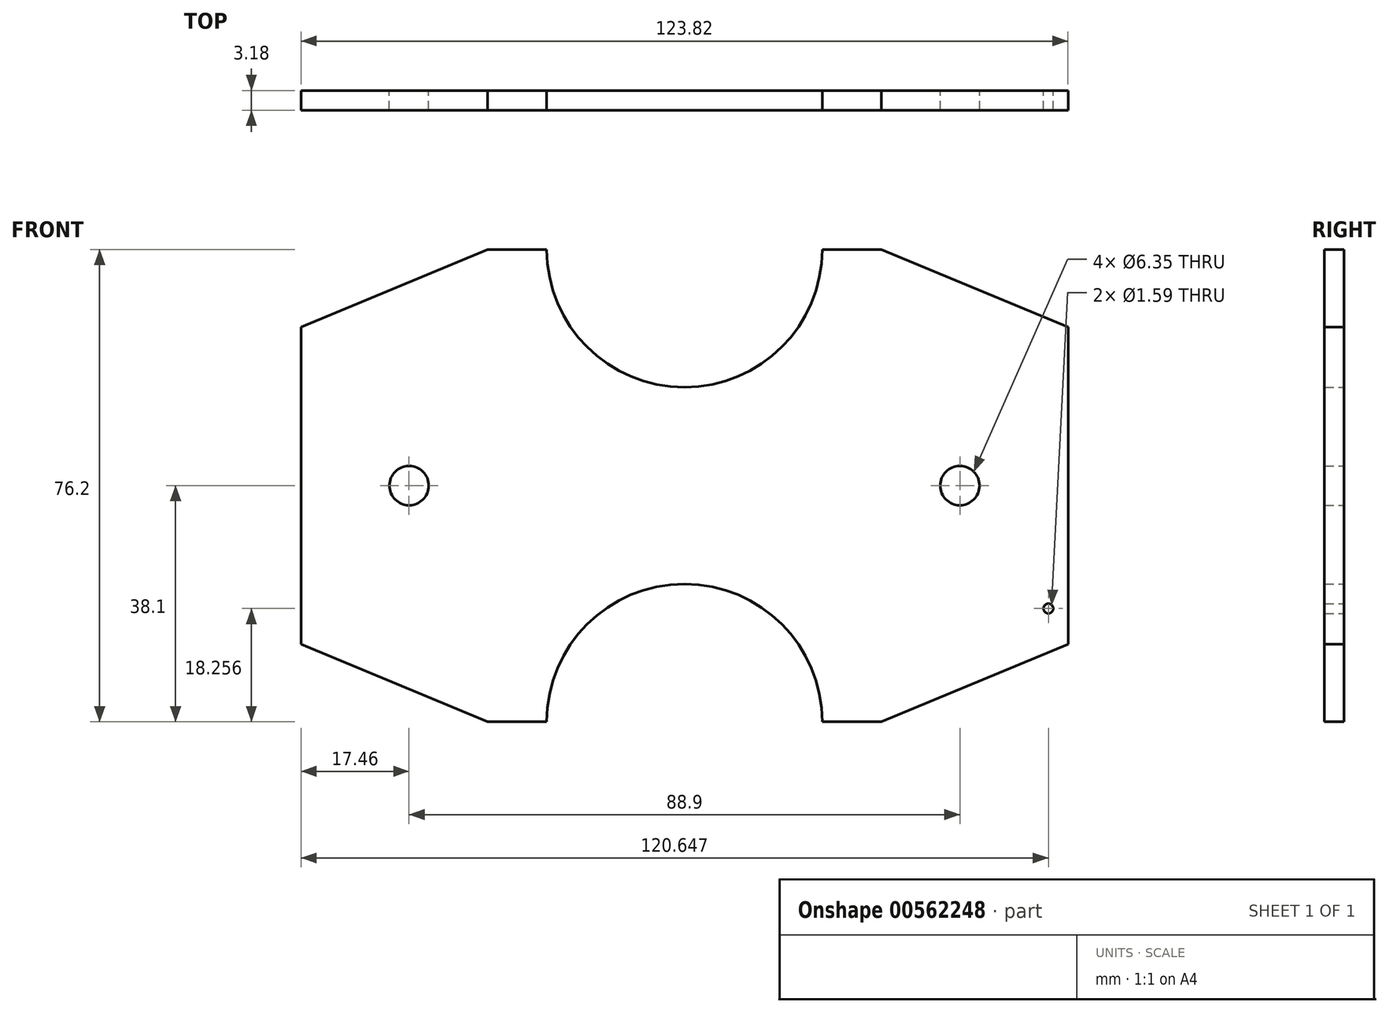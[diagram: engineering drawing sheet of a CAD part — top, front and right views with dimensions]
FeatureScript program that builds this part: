
annotation { "Feature Type Name" : "Feature", "Feature Type Description" : "" }
export const myFeature = defineFeature(function(context is Context, id is Id, definition is map)
    precondition{}
    {
        {
            var Q0;
            Q0=qCreatedBy(makeId("Front.planeOp"),FACE);
            var sketch = newSketch(context, id + "F0", { "sketchPlane" : qUnion([Q0])});
            skLineSegment(sketch, "E0.bottom", {"start": v(-31.75, 38.1) * mm, "end": v(-22.23, 38.1) * mm});
            skLineSegment(sketch, "E0.top", {"start": v(-31.75, -38.1) * mm, "end": v(-22.23, -38.1) * mm});
            skLineSegment(sketch, "E0.left", {"start": v(-61.91, 25.6) * mm, "end": v(-61.91, -25.6) * mm});
            skLineSegment(sketch, "E0.right", {"start": v(0, 38.1) * mm, "end": v(0, -38.1) * mm, "construction": true});
            skLineSegment(sketch, "E1", {"start": v(-61.91, -25.6) * mm, "end": v(-31.75, -38.1) * mm});
            skArc(sketch, "E2", {"start": v(-22.23, 38.1) * mm, "mid": v(-15.72, 22.38) * mm, "end": v(0, 15.88) * mm});
            skLineSegment(sketch, "E3", {"start": v(-31.75, 38.1) * mm, "end": v(-61.91, 25.6) * mm});
            skArc(sketch, "E4.MirrorCS", {"start": v(-22.23, -38.1) * mm, "mid": v(-15.72, -22.38) * mm, "end": v(0, -15.88) * mm});
            skArc(sketch, "E5.MirrorCS", {"start": v(22.23, -38.1) * mm, "mid": v(15.72, -22.38) * mm, "end": v(0, -15.88) * mm});
            skLineSegment(sketch, "E6.MirrorCS", {"start": v(31.75, -38.1) * mm, "end": v(22.23, -38.1) * mm});
            skLineSegment(sketch, "E7.MirrorCS", {"start": v(61.91, -25.6) * mm, "end": v(31.75, -38.1) * mm});
            skLineSegment(sketch, "E8.MirrorCS", {"start": v(61.91, 25.6) * mm, "end": v(61.91, -25.6) * mm});
            skLineSegment(sketch, "E9.MirrorCS", {"start": v(31.75, 38.1) * mm, "end": v(61.91, 25.6) * mm});
            skLineSegment(sketch, "E10.MirrorCS", {"start": v(31.75, 38.1) * mm, "end": v(22.23, 38.1) * mm});
            skArc(sketch, "E11.MirrorCS", {"start": v(22.23, 38.1) * mm, "mid": v(15.72, 22.38) * mm, "end": v(0, 15.88) * mm});
            skCircle(sketch, "E12", {"center": v(44.45, 0) * mm, "radius": 3.18 * mm});
            skCircle(sketch, "E13", {"center": v(58.74, -19.84) * mm, "radius": 0.8 * mm});
            skCircle(sketch, "E14.MirrorC", {"center": v(-44.45, 0) * mm, "radius": 3.18 * mm});
            skSolve(sketch);
        }
        {
            var Q0;
            Q0 = qSketchRegion(id + "F0", true);
            extrude(context, id + "F1", {"entities" : qUnion([Q0]), "depth" : 3.17 * mm, "offsetDistance" : 25.4 * mm});
        }
    });
